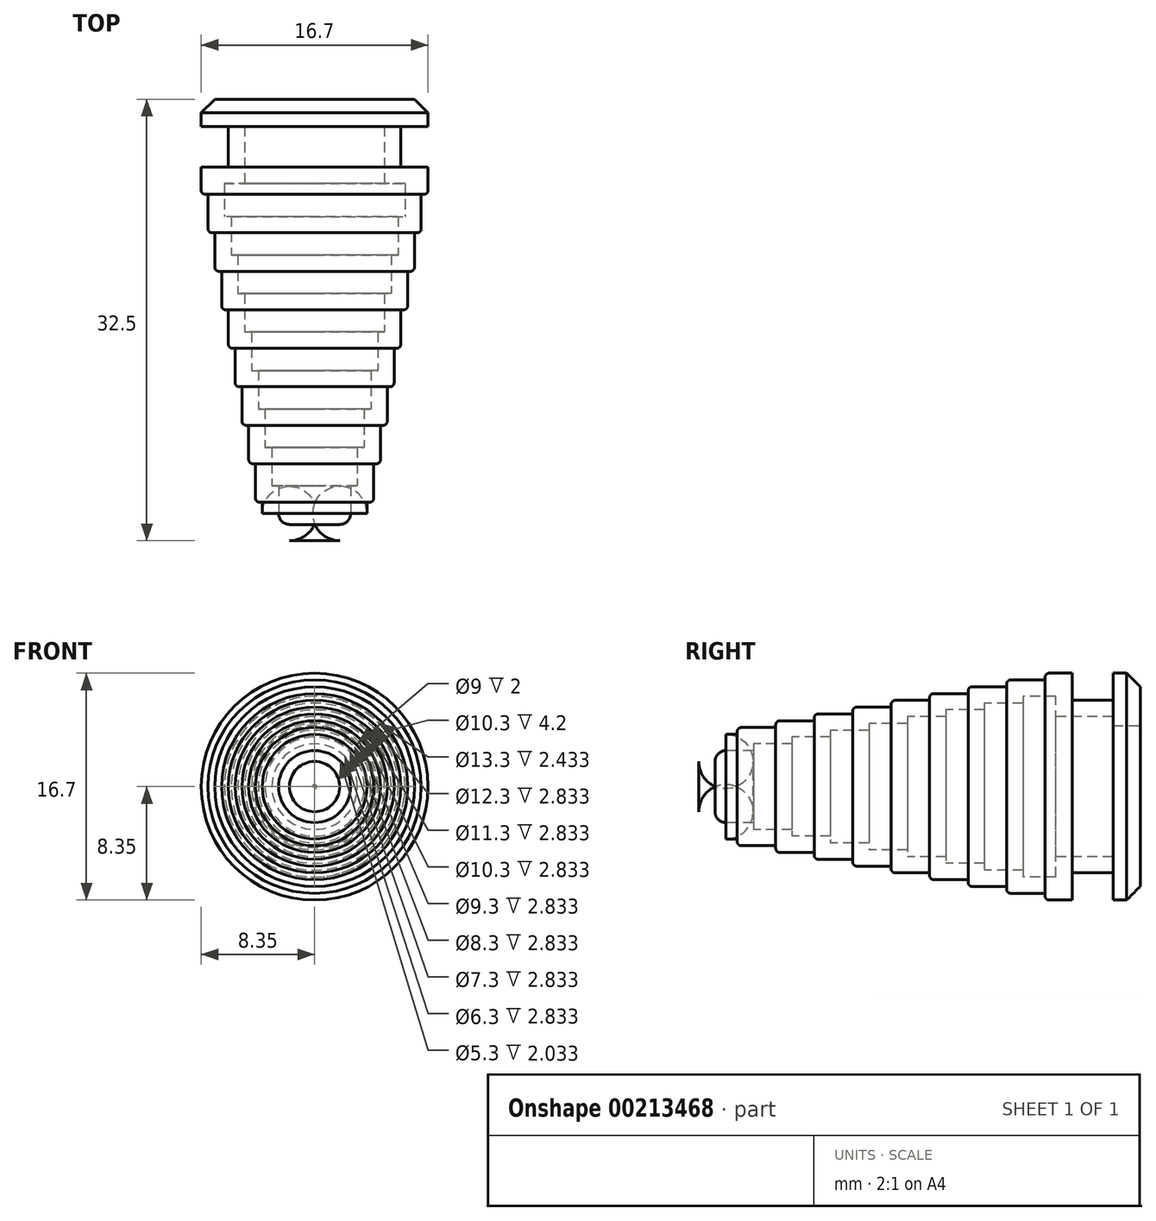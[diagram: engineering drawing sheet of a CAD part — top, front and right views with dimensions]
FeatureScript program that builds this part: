
annotation { "Feature Type Name" : "Feature", "Feature Type Description" : "" }
export const myFeature = defineFeature(function(context is Context, id is Id, definition is map)
    precondition{}
    {
        {
            var Q0;
            Q0=qCreatedBy(makeId("Right.planeOp"),FACE);
            var sketch = newSketch(context, id + "F0", { "sketchPlane" : qUnion([Q0])});
            skLineSegment(sketch, "E0", {"start": v(0, 0) * mm, "end": v(0, 8.35) * mm});
            skLineSegment(sketch, "E1", {"start": v(0, 8.35) * mm, "end": v(-2, 8.35) * mm});
            skLineSegment(sketch, "E2", {"start": v(-2, 8.35) * mm, "end": v(-2, 6.35) * mm});
            skLineSegment(sketch, "E3", {"start": v(-2, 6.35) * mm, "end": v(-5, 6.35) * mm});
            skLineSegment(sketch, "E4", {"start": v(-5, 6.35) * mm, "end": v(-5, 8.35) * mm});
            skLineSegment(sketch, "E5", {"start": v(-5, 8.35) * mm, "end": v(-7, 8.35) * mm});
            skLineSegment(sketch, "E6", {"start": v(-7, 8.35) * mm, "end": v(-7, 7.85) * mm});
            skLineSegment(sketch, "E7", {"start": v(-7, 7.85) * mm, "end": v(-9.83, 7.85) * mm});
            skLineSegment(sketch, "E8", {"start": v(-9.83, 7.85) * mm, "end": v(-9.83, 7.35) * mm});
            skLineSegment(sketch, "E9", {"start": v(-9.83, 7.35) * mm, "end": v(-12.67, 7.35) * mm});
            skLineSegment(sketch, "E10", {"start": v(-12.67, 7.35) * mm, "end": v(-12.67, 6.85) * mm});
            skLineSegment(sketch, "E11", {"start": v(-12.67, 6.85) * mm, "end": v(-15.5, 6.85) * mm});
            skLineSegment(sketch, "E12", {"start": v(-15.5, 6.85) * mm, "end": v(-15.5, 6.35) * mm});
            skLineSegment(sketch, "E13", {"start": v(-15.5, 6.35) * mm, "end": v(-18.33, 6.35) * mm});
            skLineSegment(sketch, "E14", {"start": v(-18.33, 6.35) * mm, "end": v(-18.33, 5.85) * mm});
            skLineSegment(sketch, "E15", {"start": v(-18.33, 5.85) * mm, "end": v(-21.17, 5.85) * mm});
            skLineSegment(sketch, "E16", {"start": v(-21.17, 5.85) * mm, "end": v(-21.17, 5.35) * mm});
            skLineSegment(sketch, "E17", {"start": v(-21.17, 5.35) * mm, "end": v(-24, 5.35) * mm});
            skLineSegment(sketch, "E18", {"start": v(-24, 5.35) * mm, "end": v(-24, 4.85) * mm});
            skLineSegment(sketch, "E19", {"start": v(-24, 4.85) * mm, "end": v(-26.83, 4.85) * mm});
            skLineSegment(sketch, "E20", {"start": v(-26.83, 4.85) * mm, "end": v(-26.83, 4.35) * mm});
            skLineSegment(sketch, "E21", {"start": v(-26.83, 4.35) * mm, "end": v(-29.67, 4.35) * mm});
            skLineSegment(sketch, "E22", {"start": v(-29.67, 4.35) * mm, "end": v(-29.67, 3.85) * mm});
            skLineSegment(sketch, "E23", {"start": v(-29.67, 3.85) * mm, "end": v(-32.5, 3.85) * mm});
            skLineSegment(sketch, "E24", {"start": v(-32.5, 3.85) * mm, "end": v(-32.5, 0) * mm});
            skLineSegment(sketch, "E25", {"start": v(-32.5, 0) * mm, "end": v(0, 0) * mm});
            skSolve(sketch);
        }
        {
            var Q0;
            Q0=makeQuery(id+"F0.imprint","IMPRINT",FACE,{"disambiguationData":[TD([[makeQuery(id+"F0.imprint","IMPRINT",EDGE,{"derivedFrom":sQuery(id+"F0.wireOp",EDGE,"E0")}),1.0]])]});
            var Q1;
            Q1=sQuery(id+"F0.wireOp",EDGE,"E25");
            revolve(context, id + "F1", {"entities" : qUnion([Q0]), "axis" : qUnion([Q1]), "revolveType" : RevolveType.FULL});
        }
        {
            var Q0;
            Q0=makeQuery(id+"F1.opRevolve","SWEPT_FACE",FACE,{"disambiguationData":[OSD([sQuery(id+"F0.wireOp",EDGE,"E0")])]});
            var sketch = newSketch(context, id + "F2", { "sketchPlane" : qUnion([Q0])});
            skCircle(sketch, "E26", {"center": v(0, 0) * mm, "radius": 4.5 * mm});
            skSolve(sketch);
        }
        {
            var Q0;
            Q0=makeQuery(id+"F2.imprint","IMPRINT",FACE,{"disambiguationData":[TD([[makeQuery(id+"F2.imprint","IMPRINT",EDGE,{"derivedFrom":sQuery(id+"F2.wireOp",EDGE,"E26")}),1.0]])]});
            extrude(context, id + "F3", {"entities" : qUnion([Q0]), "operationType" : NewBodyOperationType.REMOVE, "oppositeDirection" : true, "depth" : 2 * mm});
        }
        {
            var Q0;
            Q0=makeQuery(id+"F1.opRevolve","SWEPT_EDGE",EDGE,{"disambiguationData":[OSD([sQuery(id+"F0.wireOp",EDGE,"E23"),sQuery(id+"F0.wireOp",EDGE,"E24")])]});
            fillet(context, id + "F4", {"entities" : qUnion([Q0]), "radius" : 2 * mm, "tangentPropagation" : true, "allowEdgeOverflow" : false});
        }
        {
            var Q0;
            Q0=makeQuery(id+"F1.opRevolve","SWEPT_EDGE",EDGE,{"disambiguationData":[OSD([sQuery(id+"F0.wireOp",EDGE,"E5"),sQuery(id+"F0.wireOp",EDGE,"E6")])]});
            var Q1;
            Q1=makeQuery(id+"F1.opRevolve","SWEPT_EDGE",EDGE,{"disambiguationData":[OSD([sQuery(id+"F0.wireOp",EDGE,"E7"),sQuery(id+"F0.wireOp",EDGE,"E8")])]});
            var Q2;
            Q2=makeQuery(id+"F1.opRevolve","SWEPT_EDGE",EDGE,{"disambiguationData":[OSD([sQuery(id+"F0.wireOp",EDGE,"E9"),sQuery(id+"F0.wireOp",EDGE,"E10")])]});
            var Q3;
            Q3=makeQuery(id+"F1.opRevolve","SWEPT_EDGE",EDGE,{"disambiguationData":[OSD([sQuery(id+"F0.wireOp",EDGE,"E11"),sQuery(id+"F0.wireOp",EDGE,"E12")])]});
            var Q4;
            Q4=makeQuery(id+"F1.opRevolve","SWEPT_EDGE",EDGE,{"disambiguationData":[OSD([sQuery(id+"F0.wireOp",EDGE,"E13"),sQuery(id+"F0.wireOp",EDGE,"E14")])]});
            var Q5;
            Q5=makeQuery(id+"F1.opRevolve","SWEPT_EDGE",EDGE,{"disambiguationData":[OSD([sQuery(id+"F0.wireOp",EDGE,"E15"),sQuery(id+"F0.wireOp",EDGE,"E16")])]});
            var Q6;
            Q6=makeQuery(id+"F1.opRevolve","SWEPT_EDGE",EDGE,{"disambiguationData":[OSD([sQuery(id+"F0.wireOp",EDGE,"E17"),sQuery(id+"F0.wireOp",EDGE,"E18")])]});
            var Q7;
            Q7=makeQuery(id+"F1.opRevolve","SWEPT_EDGE",EDGE,{"disambiguationData":[OSD([sQuery(id+"F0.wireOp",EDGE,"E19"),sQuery(id+"F0.wireOp",EDGE,"E20")])]});
            var Q8;
            Q8=makeQuery(id+"F1.opRevolve","SWEPT_EDGE",EDGE,{"disambiguationData":[OSD([sQuery(id+"F0.wireOp",EDGE,"E21"),sQuery(id+"F0.wireOp",EDGE,"E22")])]});
            fillet(context, id + "F5", {"entities" : qUnion([Q0, Q1, Q2, Q3, Q4, Q5, Q6, Q7, Q8]), "radius" : 0.3 * mm, "tangentPropagation" : true, "allowEdgeOverflow" : false});
        }
        {
            var Q0;
            Q0=makeQuery(id+"F1.opRevolve","SWEPT_EDGE",EDGE,{"disambiguationData":[OSD([sQuery(id+"F0.wireOp",EDGE,"E0"),sQuery(id+"F0.wireOp",EDGE,"E1")])]});
            chamfer(context, id + "F6", {"entities" : qUnion([Q0]), "width" : 1 * mm, "tangentPropagation" : true});
        }
        {
            var Q0;
            Q0=makeQuery(id+"F3.boolean.opBoolean","COPY",FACE,{"derivedFrom":makeQuery(id+"F3.opExtrude","CAP_FACE",FACE,{"disambiguationData":[OSD([sQuery(id+"F2.wireOp",EDGE,"E26")])],"isStart":false})});
            shell(context, id + "F7", {"entities" : qUnion([Q0]), "thickness" : 1.2 * mm});
        }
    });
